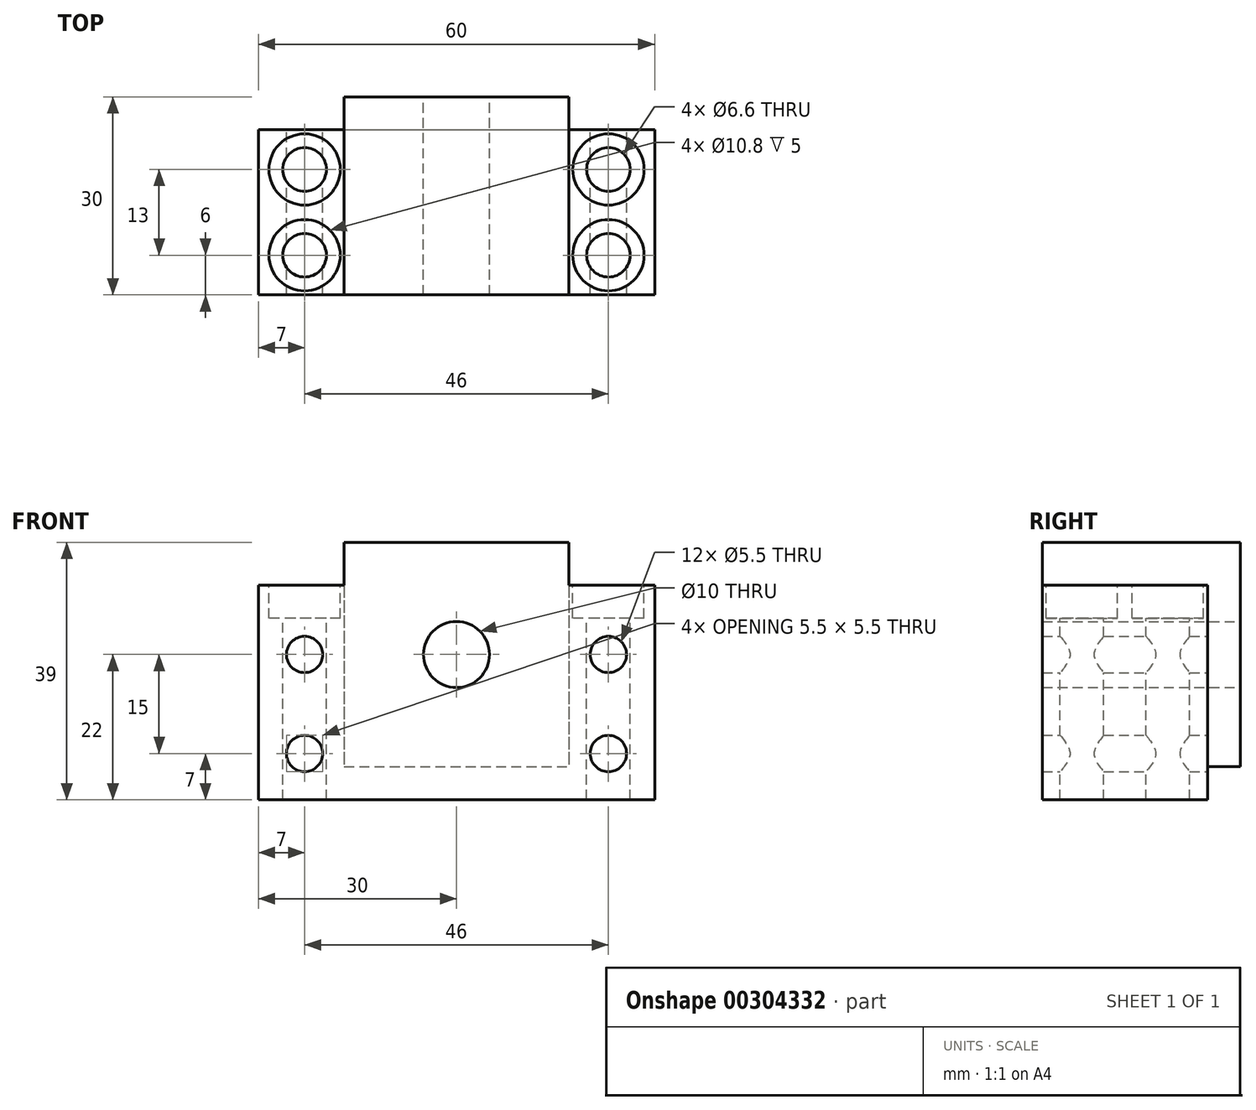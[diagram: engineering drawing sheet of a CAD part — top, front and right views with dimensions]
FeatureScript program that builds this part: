
annotation { "Feature Type Name" : "Feature", "Feature Type Description" : "" }
export const myFeature = defineFeature(function(context is Context, id is Id, definition is map)
    precondition{}
    {
        {
            var Q0;
            Q0=qCreatedBy(makeId("Front.planeOp"),FACE);
            var sketch = newSketch(context, id + "F0", { "sketchPlane" : qUnion([Q0])});
            skCircle(sketch, "E0", {"center": v(0, 0) * mm, "radius": 12.5 * mm, "construction": true});
            skCircle(sketch, "E1", {"center": v(0, 0) * mm, "radius": 5 * mm});
            skLineSegment(sketch, "E2.bottom", {"start": v(-17, 17) * mm, "end": v(17, 17) * mm});
            skLineSegment(sketch, "E2.top", {"start": v(-17, -17) * mm, "end": v(17, -17) * mm});
            skLineSegment(sketch, "E2.left", {"start": v(-17, 17) * mm, "end": v(-17, -17) * mm});
            skLineSegment(sketch, "E2.right", {"start": v(17, 17) * mm, "end": v(17, -17) * mm});
            skLineSegment(sketch, "E3.bottom", {"start": v(-30, 10.5) * mm, "end": v(30, 10.5) * mm});
            skLineSegment(sketch, "E3.top", {"start": v(-30, -22) * mm, "end": v(30, -22) * mm});
            skLineSegment(sketch, "E3.left", {"start": v(-30, 10.5) * mm, "end": v(-30, -22) * mm});
            skLineSegment(sketch, "E3.right", {"start": v(30, 10.5) * mm, "end": v(30, -22) * mm});
            skLineSegment(sketch, "E4", {"start": v(-30, -5.75) * mm, "end": v(30, -5.75) * mm, "construction": true});
            skLineSegment(sketch, "E5", {"start": v(0, -22) * mm, "end": v(0, 10.5) * mm, "construction": true});
            skLineSegment(sketch, "E6", {"start": v(0, 17) * mm, "end": v(0, -17) * mm, "construction": true});
            skLineSegment(sketch, "E7", {"start": v(-17, 0) * mm, "end": v(17, 0) * mm, "construction": true});
            skLineSegment(sketch, "E8", {"start": v(-23, 10.5) * mm, "end": v(-23, -22) * mm, "construction": true});
            skLineSegment(sketch, "E9", {"start": v(23, -22) * mm, "end": v(23, 10.5) * mm, "construction": true});
            skLineSegment(sketch, "E10", {"start": v(30, 0) * mm, "end": v(-30, 0) * mm, "construction": true});
            skLineSegment(sketch, "E11", {"start": v(30, -15) * mm, "end": v(-30, -15) * mm, "construction": true});
            skCircle(sketch, "E12", {"center": v(-23, 0) * mm, "radius": 2.75 * mm});
            skCircle(sketch, "E13", {"center": v(-23, -15) * mm, "radius": 2.75 * mm});
            skCircle(sketch, "E14", {"center": v(23, -15) * mm, "radius": 2.75 * mm});
            skCircle(sketch, "E15", {"center": v(23, 0) * mm, "radius": 2.75 * mm});
            skSolve(sketch);
        }
        {
            var Q0;
            Q0 = qSketchRegion(id + "F0", true);
            extrude(context, id + "F1", {"entities" : qUnion([Q0]), "depth" : 25 * mm});
        }
        {
            var Q0;
            {var subQ0=sQuery(id+"F0.wireOp",EDGE,"E2.bottom");Q0=makeQuery(id+"F0.imprint","IMPRINT",FACE,{"disambiguationData":[TD([[makeQuery(id+"F0.imprint","IMPRINT",EDGE,{"derivedFrom":subQ0}),-1.0]])]});}
            var Q1;
            Q1=makeQuery(id+"F0.imprint","IMPRINT",FACE,{"disambiguationData":[TD([[makeQuery(id+"F0.imprint","IMPRINT",EDGE,{"derivedFrom":sQuery(id+"F0.wireOp",EDGE,"E1")}),-1.0]])]});
            extrude(context, id + "F2", {"entities" : qUnion([Q0, Q1]), "operationType" : NewBodyOperationType.ADD, "oppositeDirection" : true, "depth" : 5 * mm});
        }
        {
            var Q0;
            {var subQ0=sQuery(id+"F0.wireOp",EDGE,"E3.bottom");Q0=makeQuery(id+"F1.opExtrude","SWEPT_FACE",FACE,{"disambiguationData":[OSD([subQ0]),TDD([makeQuery(id+"F0.imprint","IMPRINT",EDGE,{"disambiguationData":[TD([[makeQuery(id+"F0.imprint","INTERSECT",VERTEX,{"derivedFrom":[subQ0,sQuery(id+"F0.wireOp",EDGE,"E3.right")]}),1.0]])],"derivedFrom":subQ0})])]});}
            var sketch = newSketch(context, id + "F3", { "sketchPlane" : qUnion([Q0])});
            skLineSegment(sketch, "E16", {"start": v(-30.03, -6) * mm, "end": v(30, -6) * mm, "construction": true});
            skLineSegment(sketch, "E17", {"start": v(-30.03, -19) * mm, "end": v(30, -19) * mm, "construction": true});
            skLineSegment(sketch, "E18", {"start": v(23, 0) * mm, "end": v(23, -25) * mm, "construction": true});
            skLineSegment(sketch, "E19", {"start": v(-23, 0) * mm, "end": v(-23, -25) * mm, "construction": true});
            skLineSegment(sketch, "E20", {"start": v(0, 4.97) * mm, "end": v(0, -25) * mm, "construction": true});
            skPoint(sketch, "E21", {"position": v(-23, -6) * mm});
            skPoint(sketch, "E22", {"position": v(-23, -19) * mm});
            skPoint(sketch, "E23", {"position": v(23, -19) * mm});
            skPoint(sketch, "E24", {"position": v(23, -6) * mm});
            skSolve(sketch);
        }
        {
            var Q0;
            Q0=sQuery(id+"F3.wireOp",VERTEX,"E21");
            var Q1;
            Q1=sQuery(id+"F3.wireOp",VERTEX,"E22");
            var Q2;
            Q2=sQuery(id+"F3.wireOp",VERTEX,"E23");
            var Q3;
            Q3=sQuery(id+"F3.wireOp",VERTEX,"E24");
            var Q4;
            Q4=makeQuery(id+"F1.opExtrude","SWEPT_BODY",BODY,{"disambiguationData":[OSD([sQuery(id+"F0.wireOp",EDGE,"E1"),sQuery(id+"F0.wireOp",EDGE,"E2.bottom"),sQuery(id+"F0.wireOp",EDGE,"E2.left"),sQuery(id+"F0.wireOp",EDGE,"E2.right"),sQuery(id+"F0.wireOp",EDGE,"E3.bottom"),sQuery(id+"F0.wireOp",EDGE,"E3.top"),sQuery(id+"F0.wireOp",EDGE,"E3.left"),sQuery(id+"F0.wireOp",EDGE,"E3.right"),sQuery(id+"F0.wireOp",EDGE,"E12"),sQuery(id+"F0.wireOp",EDGE,"E13"),sQuery(id+"F0.wireOp",EDGE,"E14"),sQuery(id+"F0.wireOp",EDGE,"E15")])]});
            hole(context, id + "F4", {"style" : HoleStyle.C_BORE, "endStyle" : HoleEndStyle.THROUGH, "holeDiameter" : 6.6 * mm, "cBoreDiameter" : 10.8 * mm, "cBoreDepth" : 5 * mm, "tappedDepth" : 9.6 * mm, "tapClearance" : 3, "locations" : qUnion([Q0, Q1, Q2, Q3]), "scope" : qUnion([Q4])});
        }
    });
